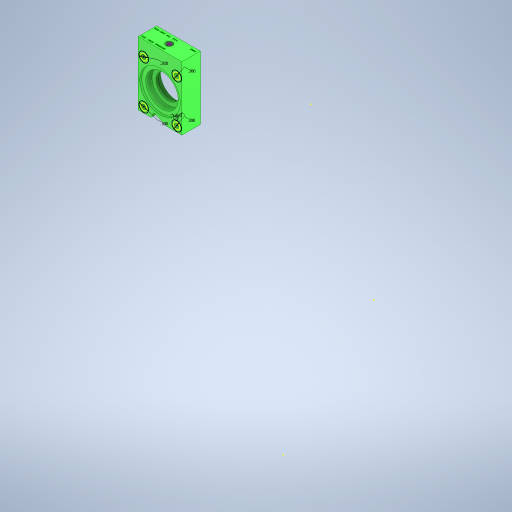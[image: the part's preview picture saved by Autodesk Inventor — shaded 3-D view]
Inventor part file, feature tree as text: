
AUTODESK INVENTOR PART (.ipt)
format: ipt  version: 2024.1 (Build 281209000, 209)  size: 712,704 bytes
history: native  units: in
note: dims shown in document units (in); Inventor stores cm internally (conversion verified against a paired STEP export)
features: hole x7, extrude x5, sketch x4, fillet x1
ambient origin geometry x8: Origin, YZ Plane, XZ Plane, XY Plane, X Axis, Y Axis, Z Axis, Center Point
bodies: Solid1 (feature_tree)
feature tree (17):
  extrude  "Extrusion1"  Depth=0.4in TaperAngle=0.0deg
  extrude  "Extrusion2"  Depth=0.25in
  extrude  "Extrusion3"  Depth=0.25in
  hole  "Hole1"  [1 undecoded]
  hole  "Hole2"  [1 undecoded]
  extrude  "Extrusion4"  Depth=0.25in
  hole  "Hole5"  [1 undecoded]
  hole  "Hole6"  [1 undecoded]
  fillet  "Fillet1"  Radius=1.0in
  sketch  "Sketch7"  dims[d13=0.06in d14=0.75in d15=0.507in d16=0.25in d17=0.5635in d18=1.0in d19=0.8108in d20=0.4583in d21=0.29in d22=0.04in d23=0.75in d24=0.507in d25=0.25in d26=0.5635in d27=1.0in d28=0.8108in d29=0.213in d30=0.75in d31=0.507in d32=0.25in d33=0.5635in d34=0.25in d35=0.0in d36=0.75in d38=135.0deg d39=0.4583in d40=112.5deg d41=0.25in d42=1.0in d43=0.0in d44=0.29in d45=0.196in d46=0.211in d47=0.25in d48=0.375in d49=0.25in d50=0.5635in d51=0.25in d52=0.0in d53=0.06in d54=0.75in d55=0.375in d56=0.25in d57=0.5635in d58=0.6in d59=0.8108in d60=0.0312in d61=0.13in d62=0.6in d63=0.375in d64=0.25in d65=0.5635in d66=0.484in d67=0.0in d68=0.5in d69=0.0in d70=0.3in d71=0.3in d72=0.3in d73=0.3in]
  extrude  "Extrusion5"  Depth=0.25in
  hole  "Hole7"  [1 undecoded]
  hole  "Hole3"  [1 undecoded]
  hole  "Hole4"  [1 undecoded]
  sketch  "Sketch1"  dims[d0=0.5in d1=0.0in d2=0.4in d3=0.0in]
  sketch  "Sketch2"  dims[d4=0.6in d5=0.0in]
  sketch  "Sketch5"  dims[d6=0.211in d7=0.25in d8=0.507in d9=0.25in d10=0.5635in d11=0.25in d12=0.0in]
note: 7 required parameter values undecoded (feature->parameter linkage not recoverable at this tier; creation-order binding heuristic only, values carry confidence <= 0.55)
